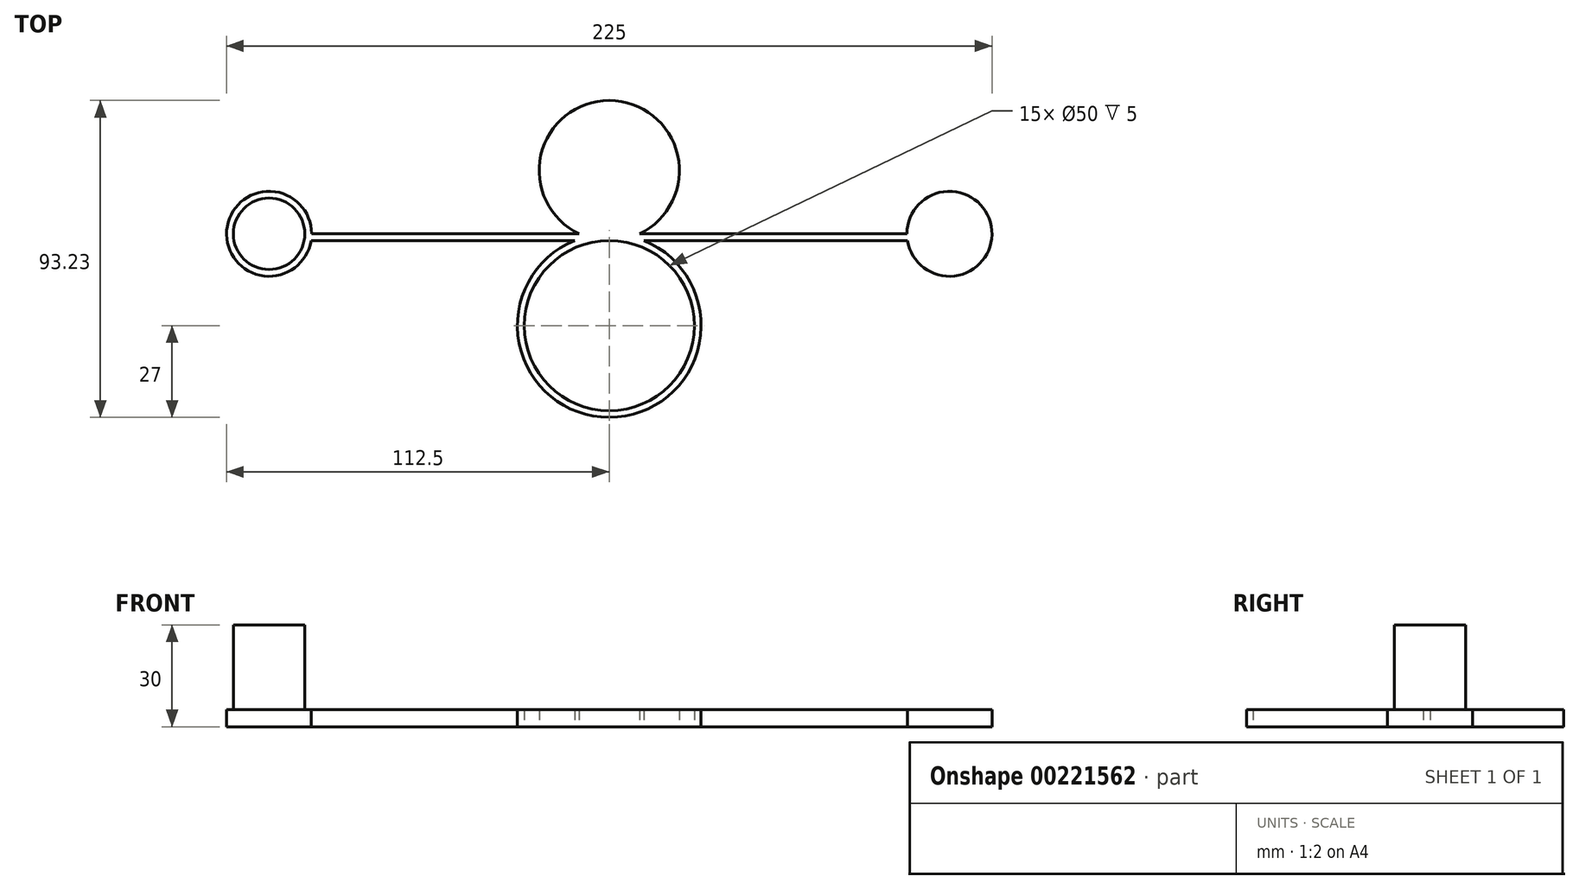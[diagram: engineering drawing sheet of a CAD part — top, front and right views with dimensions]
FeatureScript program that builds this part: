
annotation { "Feature Type Name" : "Feature", "Feature Type Description" : "" }
export const myFeature = defineFeature(function(context is Context, id is Id, definition is map)
    precondition{}
    {
        {
            var Q0;
            Q0=qCreatedBy(makeId("Top.planeOp"),FACE);
            var sketch = newSketch(context, id + "F0", { "sketchPlane" : qUnion([Q0])});
            skCircle(sketch, "E0", {"center": v(0, 0) * mm, "radius": 25 * mm});
            skArc(sketch, "E1", {"start": v(-10.2, 25) * mm, "mid": v(0, -27) * mm, "end": v(10.2, 25) * mm});
            skLineSegment(sketch, "E2", {"start": v(0, 27) * mm, "end": v(100, 27) * mm});
            skLineSegment(sketch, "E3", {"start": v(100, 27) * mm, "end": v(100, 25) * mm});
            skLineSegment(sketch, "E4", {"start": v(100, 25) * mm, "end": v(10.2, 25) * mm});
            skLineSegment(sketch, "E5.MirrorCS", {"start": v(0, 27) * mm, "end": v(-100, 27) * mm});
            skLineSegment(sketch, "E6.MirrorCS", {"start": v(-100, 27) * mm, "end": v(-100, 25) * mm});
            skLineSegment(sketch, "E7.MirrorCS", {"start": v(-100, 25) * mm, "end": v(-10.2, 25) * mm});
            skCircle(sketch, "E8", {"center": v(100, 27) * mm, "radius": 12.5 * mm});
            skCircle(sketch, "E9.MirrorC", {"center": v(-100, 27) * mm, "radius": 12.5 * mm});
            skCircle(sketch, "E10", {"center": v(0, 45.61) * mm, "radius": 20.61 * mm});
            skSolve(sketch);
        }
        {
            var Q0;
            Q0=makeQuery(id+"F0.imprint","IMPRINT",FACE,{"disambiguationData":[TD([[makeQuery(id+"F0.imprint","IMPRINT",EDGE,{"derivedFrom":sQuery(id+"F0.wireOp",EDGE,"E0")}),-1.0]])]});
            var Q1;
            {var subQ0=sQuery(id+"F0.wireOp",EDGE,"E3");Q1=makeQuery(id+"F0.imprint","IMPRINT",FACE,{"disambiguationData":[TD([[makeQuery(id+"F0.imprint","IMPRINT",EDGE,{"derivedFrom":subQ0}),1.0]])]});}
            var Q2;
            {var subQ0=sQuery(id+"F0.wireOp",EDGE,"E3");Q2=makeQuery(id+"F0.imprint","IMPRINT",FACE,{"disambiguationData":[TD([[makeQuery(id+"F0.imprint","IMPRINT",EDGE,{"derivedFrom":subQ0}),-1.0]])]});}
            var Q3;
            {var subQ0=sQuery(id+"F0.wireOp",EDGE,"E6.MirrorCS");Q3=makeQuery(id+"F0.imprint","IMPRINT",FACE,{"disambiguationData":[TD([[makeQuery(id+"F0.imprint","IMPRINT",EDGE,{"derivedFrom":subQ0}),-1.0]])]});}
            var Q4;
            {var subQ0=sQuery(id+"F0.wireOp",EDGE,"E5.MirrorCS");var subQ1=sQuery(id+"F0.wireOp",EDGE,"E2");var subQ2=makeQuery(id+"F0.imprint","INTERSECT",VERTEX,{"derivedFrom":[subQ1,subQ0]});Q4=makeQuery(id+"F0.imprint","IMPRINT",FACE,{"disambiguationData":[TD([[makeQuery(id+"F0.imprint","IMPRINT",EDGE,{"disambiguationData":[TD([[subQ2,-1.0]])],"derivedFrom":subQ1}),-1.0]])]});}
            var Q5;
            {var subQ0=sQuery(id+"F0.wireOp",EDGE,"E5.MirrorCS");var subQ1=sQuery(id+"F0.wireOp",EDGE,"E2");var subQ2=makeQuery(id+"F0.imprint","INTERSECT",VERTEX,{"derivedFrom":[subQ1,subQ0]});Q5=makeQuery(id+"F0.imprint","IMPRINT",FACE,{"disambiguationData":[TD([[makeQuery(id+"F0.imprint","IMPRINT",EDGE,{"disambiguationData":[TD([[subQ2,-1.0]])],"derivedFrom":subQ1}),1.0]])]});}
            var Q6;
            {var subQ0=sQuery(id+"F0.wireOp",EDGE,"E6.MirrorCS");Q6=makeQuery(id+"F0.imprint","IMPRINT",FACE,{"disambiguationData":[TD([[makeQuery(id+"F0.imprint","IMPRINT",EDGE,{"derivedFrom":subQ0}),1.0]])]});}
            extrude(context, id + "F1", {"entities" : qUnion([Q0, Q1, Q2, Q3, Q4, Q5, Q6]), "depth" : 30 * mm});
        }
        {
            var Q0;
            Q0=makeQuery(id+"F1.opExtrude","CAP_FACE",FACE,{"disambiguationData":[OSD([sQuery(id+"F0.wireOp",EDGE,"E0"),sQuery(id+"F0.wireOp",EDGE,"E1"),sQuery(id+"F0.wireOp",EDGE,"E2"),sQuery(id+"F0.wireOp",EDGE,"E4"),sQuery(id+"F0.wireOp",EDGE,"E5.MirrorCS"),sQuery(id+"F0.wireOp",EDGE,"E7.MirrorCS"),sQuery(id+"F0.wireOp",EDGE,"E8"),sQuery(id+"F0.wireOp",EDGE,"E9.MirrorC"),sQuery(id+"F0.wireOp",EDGE,"E10")])],"isStart":false});
            var sketch = newSketch(context, id + "F2", { "sketchPlane" : qUnion([Q0])});
            skCircle(sketch, "E11", {"center": v(100, 27) * mm, "radius": 10.5 * mm});
            skCircle(sketch, "E12.MirrorC", {"center": v(-100, 27) * mm, "radius": 10.5 * mm});
            skCircle(sketch, "E13", {"center": v(0, 45.61) * mm, "radius": 15 * mm});
            skSolve(sketch);
        }
        {
            var Q0;
            Q0=makeQuery(id+"F2.imprint","IMPRINT",FACE,{"disambiguationData":[TD([[makeQuery(id+"F2.imprint","IMPRINT",EDGE,{"derivedFrom":sQuery(id+"F2.wireOp",EDGE,"E11")}),1.0]])]});
            var Q1;
            Q1=makeQuery(id+"F2.imprint","IMPRINT",FACE,{"disambiguationData":[TD([[makeQuery(id+"F2.imprint","IMPRINT",EDGE,{"derivedFrom":sQuery(id+"F2.wireOp",EDGE,"E12.MirrorC")}),-1.0]])]});
            extrude(context, id + "F3", {"entities" : qUnion([Q0, Q1]), "operationType" : NewBodyOperationType.REMOVE, "oppositeDirection" : true, "depth" : 25 * mm});
        }
        {
            var Q0;
            Q0=makeQuery(id+"F2.imprint","IMPRINT",FACE,{"disambiguationData":[TD([[makeQuery(id+"F2.imprint","IMPRINT",EDGE,{"derivedFrom":sQuery(id+"F2.wireOp",EDGE,"E13")}),1.0]])]});
            extrude(context, id + "F4", {"entities" : qUnion([Q0]), "operationType" : NewBodyOperationType.REMOVE, "oppositeDirection" : true, "depth" : 25 * mm});
        }
    });
